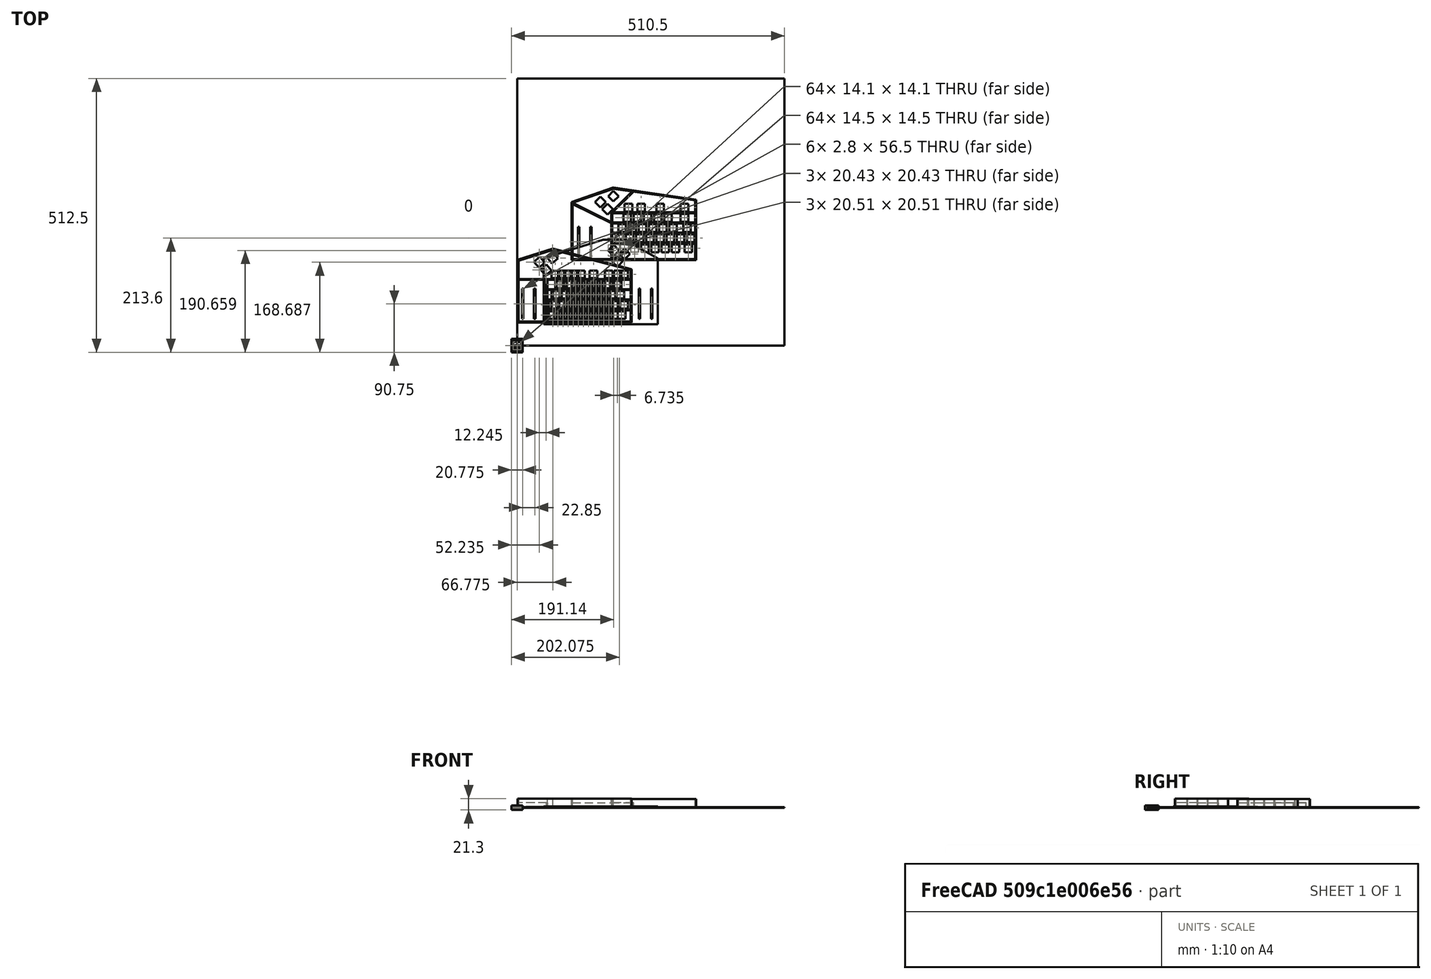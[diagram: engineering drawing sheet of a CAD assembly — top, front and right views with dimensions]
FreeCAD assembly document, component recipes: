
FREECAD ASSEMBLY — COMPONENT RECIPES ("keyboard")

This assembly document has 5 components, labeled P0..P4 below (a component is one placed body or linked part). 4 of them carry a construction recipe — the FreeCAD feature program that regenerates the part from scratch, quoted from this document or its linked companion documents; the rest are supplied as boundary geometry only. No exploded tour is included for this assembly.
COMPONENT P0 — recipe-attached ("Body", modeled in this document).
Construction recipe (the document's own serialized feature program — sketch geometry with constraints, then the solid features built on it; lengths are millimeters unless a unit is written):

FEATURE [Sketcher::SketchObject] Sketch
  FullyConstrained = true
  MapMode = 5
  Support = -> [XY_Plane001]
  sketch-geometry (8):
    g0: LineSegment StartX=-7.5 StartY=7.5 StartZ=0 EndX=7.5 EndY=7.5 EndZ=0
    g1: LineSegment StartX=7.5 StartY=7.5 StartZ=0 EndX=7.5 EndY=-7.5 EndZ=0
    g2: LineSegment StartX=7.5 StartY=-7.5 StartZ=0 EndX=-7.5 EndY=-7.5 EndZ=0
    g3: LineSegment StartX=-7.5 StartY=-7.5 StartZ=0 EndX=-7.5 EndY=7.5 EndZ=0
    g4: LineSegment StartX=-10.5 StartY=10.5 StartZ=0 EndX=10.5 EndY=10.5 EndZ=0
    g5: LineSegment StartX=10.5 StartY=10.5 StartZ=0 EndX=10.5 EndY=-10.5 EndZ=0
    g6: LineSegment StartX=10.5 StartY=-10.5 StartZ=0 EndX=-10.5 EndY=-10.5 EndZ=0
    g7: LineSegment StartX=-10.5 StartY=-10.5 StartZ=0 EndX=-10.5 EndY=10.5 EndZ=0
  constraints (20):
    c: Coincident(g0,g1)
    c: Coincident(g1,g2)
    c: Coincident(g2,g3)
    c: Coincident(g3,g0)
    c: Horizontal(g2)
    c: Vertical(g1)
    c: Symmetric(g0,g0,g-2)
    c: Symmetric(g0,g2,g-1)
    c: Equal(g0,g3)
    c: DistanceX(g0,g0) = 15
    c: Coincident(g4,g5)
    c: Coincident(g5,g6)
    c: Coincident(g6,g7)
    c: Coincident(g7,g4)
    c: Horizontal(g6)
    c: Vertical(g5)
    c: Symmetric(g4,g4,g-2)
    c: Symmetric(g4,g6,g-1)
    c: Equal(g4,g7)
    c: DistanceX(g4,g0) = 3
FEATURE [PartDesign::Pad] Pad
  Direction = (0,0,1)
  Length = 2.5
  Length2 = 10
  Profile = -> Sketch
  ReferenceAxis = -> Sketch [N_Axis]
  Type = 0
FEATURE [Sketcher::SketchObject] Sketch001
  ExternalGeometry = -> [Pad]
  FullyConstrained = true
  MapMode = 5
  Placement = pos=(0,0,0) rot=(1,0,0;3.14159rad)
  Support = -> [Pad]
  expr: Constraints[11] = 4.15 / 2
  sketch-geometry (5):
    g0: LineSegment StartX=-10.5 StartY=10.5 StartZ=0 EndX=10.5 EndY=10.5 EndZ=0
    g1: LineSegment StartX=10.5 StartY=10.5 StartZ=0 EndX=10.5 EndY=-10.5 EndZ=0
    g2: LineSegment StartX=10.5 StartY=-10.5 StartZ=0 EndX=-10.5 EndY=-10.5 EndZ=0
    g3: LineSegment StartX=-10.5 StartY=-10.5 StartZ=0 EndX=-10.5 EndY=10.5 EndZ=0
    g4: Circle CenterX=0 CenterY=0 CenterZ=0 NormalX=0 NormalY=0 NormalZ=1 AngleXU=0 Radius=2.075
  constraints (12):
    c: Coincident(g0,g1)
    c: Coincident(g1,g2)
    c: Coincident(g2,g3)
    c: Coincident(g3,g0)
    c: Horizontal(g0)
    c: Horizontal(g2)
    c: Vertical(g1)
    c: Vertical(g3)
    c: Coincident(g0,g-3)
    c: Coincident(g1,g-4)
    c: Coincident(g4,g-1)
    c: Radius(g4) = 2.075
FEATURE [PartDesign::Pad] Pad001
  BaseFeature = -> Pad
  Direction = (0,0,-1)
  Length = 4
  Length2 = 10
  Profile = -> Sketch001
  ReferenceAxis = -> Sketch001 [N_Axis]
  Type = 0
FEATURE [Sketcher::SketchObject] Sketch002
  ExternalGeometry = -> [Pad001]
  FullyConstrained = true
  MapMode = 5
  Placement = pos=(0,0,2.5) rot=(0,0,1;0rad)
  Support = -> [Pad001]
  sketch-geometry (8):
    g0: LineSegment StartX=-10.5 StartY=10.5 StartZ=0 EndX=10.5 EndY=10.5 EndZ=0
    g1: LineSegment StartX=10.5 StartY=10.5 StartZ=0 EndX=10.5 EndY=-10.5 EndZ=0
    g2: LineSegment StartX=10.5 StartY=-10.5 StartZ=0 EndX=-10.5 EndY=-10.5 EndZ=0
    g3: LineSegment StartX=-10.5 StartY=-10.5 StartZ=0 EndX=-10.5 EndY=10.5 EndZ=0
    g4: LineSegment StartX=-7.25 StartY=7.25 StartZ=0 EndX=7.25 EndY=7.25 EndZ=0
    g5: LineSegment StartX=7.25 StartY=7.25 StartZ=0 EndX=7.25 EndY=-7.25 EndZ=0
    g6: LineSegment StartX=7.25 StartY=-7.25 StartZ=0 EndX=-7.25 EndY=-7.25 EndZ=0
    g7: LineSegment StartX=-7.25 StartY=-7.25 StartZ=0 EndX=-7.25 EndY=7.25 EndZ=0
  constraints (20):
    c: Coincident(g0,g1)
    c: Coincident(g1,g2)
    c: Coincident(g2,g3)
    c: Coincident(g3,g0)
    c: Horizontal(g0)
    c: Horizontal(g2)
    c: Vertical(g1)
    c: Vertical(g3)
    c: Coincident(g0,g-3)
    c: Coincident(g1,g-4)
    c: Coincident(g4,g5)
    c: Coincident(g5,g6)
    c: Coincident(g6,g7)
    c: Coincident(g7,g4)
    c: Horizontal(g6)
    c: Vertical(g5)
    c: Symmetric(g4,g4,g-2)
    c: Symmetric(g4,g6,g-1)
    c: DistanceX(g4,g4) = 14.5
    c: Equal(g7,g4)
FEATURE [PartDesign::Pad] Pad002
  BaseFeature = -> Pad001
  Direction = (0,0,1)
  Length = 2.3
  Length2 = 10
  Profile = -> Sketch002
  ReferenceAxis = -> Sketch002 [N_Axis]
  Type = 0
FEATURE [PartDesign::Chamfer] Chamfer
  Angle = 45
  Base = -> Pad002 [Edge19,Edge23,Edge11,Edge12]
  BaseFeature = -> Pad002
  ChamferType = 0
  FlipDirection = false
  Size = 3
  Size2 = 1
  SupportTransform = false
  UseAllEdges = false
FEATURE [Sketcher::SketchObject] Sketch003
  FullyConstrained = true
  MapMode = 5
  Placement = pos=(0,0,-4) rot=(1,0,0;3.14159rad)
  Support = -> [Chamfer]
  sketch-geometry (2):
    g0: Circle CenterX=4 CenterY=2.85 CenterZ=0 NormalX=0 NormalY=0 NormalZ=1 AngleXU=0 Radius=0.75
    g1: Circle CenterX=-2.9 CenterY=5 CenterZ=0 NormalX=0 NormalY=0 NormalZ=1 AngleXU=0 Radius=0.75
  constraints (6):
    c: DistanceX(g-1,g0) = 4
    c: DistanceY(g-1,g0) = 2.85
    c: Radius(g0) = 0.75
    c: DistanceX(g1,g-1) = 2.9
    c: DistanceY(g-1,g1) = 5
    c: Equal(g1,g0)
FEATURE [PartDesign::Pocket] Pocket
  BaseFeature = -> Chamfer
  Direction = (0,0,1)
  Length = 5
  Length2 = 5
  Profile = -> Sketch003
  ReferenceAxis = -> Sketch003 [N_Axis]
  Type = 1
FEATURE [PartDesign::Chamfer] Chamfer001
  Angle = 45
  Base = -> Pocket [Edge27,Edge26]
  BaseFeature = -> Pocket
  ChamferType = 1
  FlipDirection = false
  Size = 1.8
  Size2 = 3.999
  SupportTransform = false
  UseAllEdges = false
FEATURE [PartDesign::Body] Body
  Group = -> [Sketch,Pad,Sketch001,Pad001,Sketch002,Pad002,Chamfer,Sketch003,Pocket,Chamfer001]
  Origin = -> Origin001
  Tip = -> Chamfer001
COMPONENT P1 — recipe-attached ("Body001", modeled in this document).
Construction recipe (the document's own serialized feature program — sketch geometry with constraints, then the solid features built on it; lengths are millimeters unless a unit is written):

FEATURE [Sketcher::SketchObject] Sketch004
  FullyConstrained = true
  MapMode = 5
  Support = -> [XY_Plane002]
  sketch-geometry (8):
    g0: LineSegment StartX=-7.5 StartY=7.5 StartZ=0 EndX=7.5 EndY=7.5 EndZ=0
    g1: LineSegment StartX=7.5 StartY=7.5 StartZ=0 EndX=7.5 EndY=-7.5 EndZ=0
    g2: LineSegment StartX=7.5 StartY=-7.5 StartZ=0 EndX=-7.5 EndY=-7.5 EndZ=0
    g3: LineSegment StartX=-7.5 StartY=-7.5 StartZ=0 EndX=-7.5 EndY=7.5 EndZ=0
    g4: LineSegment StartX=-10.5 StartY=10.5 StartZ=0 EndX=10.5 EndY=10.5 EndZ=0
    g5: LineSegment StartX=10.5 StartY=10.5 StartZ=0 EndX=10.5 EndY=-10.5 EndZ=0
    g6: LineSegment StartX=10.5 StartY=-10.5 StartZ=0 EndX=-10.5 EndY=-10.5 EndZ=0
    g7: LineSegment StartX=-10.5 StartY=-10.5 StartZ=0 EndX=-10.5 EndY=10.5 EndZ=0
  constraints (20):
    c: Coincident(g0,g1)
    c: Coincident(g1,g2)
    c: Coincident(g2,g3)
    c: Coincident(g3,g0)
    c: Horizontal(g2)
    c: Vertical(g1)
    c: Symmetric(g0,g0,g-2)
    c: Symmetric(g0,g2,g-1)
    c: Equal(g0,g3)
    c: DistanceX(g0,g0) = 15
    c: Coincident(g4,g5)
    c: Coincident(g5,g6)
    c: Coincident(g6,g7)
    c: Coincident(g7,g4)
    c: Horizontal(g6)
    c: Vertical(g5)
    c: Symmetric(g4,g4,g-2)
    c: Symmetric(g4,g6,g-1)
    c: Equal(g4,g7)
    c: DistanceX(g4,g0) = 3
FEATURE [PartDesign::Pad] Pad003
  Direction = (0,0,1)
  Length = 2.5
  Length2 = 10
  Profile = -> Sketch004
  ReferenceAxis = -> Sketch004 [N_Axis]
  Type = 0
FEATURE [Sketcher::SketchObject] Sketch005
  ExternalGeometry = -> [Pad003]
  FullyConstrained = true
  MapMode = 5
  Placement = pos=(0,0,0) rot=(1,0,0;3.14159rad)
  Support = -> [Pad003]
  expr: Constraints[11] = 4.15 / 2
  sketch-geometry (5):
    g0: LineSegment StartX=-10.5 StartY=10.5 StartZ=0 EndX=10.5 EndY=10.5 EndZ=0
    g1: LineSegment StartX=10.5 StartY=10.5 StartZ=0 EndX=10.5 EndY=-10.5 EndZ=0
    g2: LineSegment StartX=10.5 StartY=-10.5 StartZ=0 EndX=-10.5 EndY=-10.5 EndZ=0
    g3: LineSegment StartX=-10.5 StartY=-10.5 StartZ=0 EndX=-10.5 EndY=10.5 EndZ=0
    g4: Circle CenterX=0 CenterY=0 CenterZ=0 NormalX=0 NormalY=0 NormalZ=1 AngleXU=0 Radius=2.075
  constraints (12):
    c: Coincident(g0,g1)
    c: Coincident(g1,g2)
    c: Coincident(g2,g3)
    c: Coincident(g3,g0)
    c: Horizontal(g0)
    c: Horizontal(g2)
    c: Vertical(g1)
    c: Vertical(g3)
    c: Coincident(g0,g-3)
    c: Coincident(g1,g-4)
    c: Coincident(g4,g-1)
    c: Radius(g4) = 2.075
FEATURE [PartDesign::Pad] Pad004
  BaseFeature = -> Pad003
  Direction = (0,0,-1)
  Length = 4
  Length2 = 10
  Profile = -> Sketch005
  ReferenceAxis = -> Sketch005 [N_Axis]
  Type = 0
FEATURE [Sketcher::SketchObject] Sketch006
  ExternalGeometry = -> [Pad004]
  FullyConstrained = true
  MapMode = 5
  Placement = pos=(0,0,2.5) rot=(0,0,1;0rad)
  Support = -> [Pad004]
  sketch-geometry (8):
    g0: LineSegment StartX=-10.5 StartY=10.5 StartZ=0 EndX=10.5 EndY=10.5 EndZ=0
    g1: LineSegment StartX=10.5 StartY=10.5 StartZ=0 EndX=10.5 EndY=-10.5 EndZ=0
    g2: LineSegment StartX=10.5 StartY=-10.5 StartZ=0 EndX=-10.5 EndY=-10.5 EndZ=0
    g3: LineSegment StartX=-10.5 StartY=-10.5 StartZ=0 EndX=-10.5 EndY=10.5 EndZ=0
    g4: LineSegment StartX=-7.25 StartY=7.25 StartZ=0 EndX=7.25 EndY=7.25 EndZ=0
    g5: LineSegment StartX=7.25 StartY=7.25 StartZ=0 EndX=7.25 EndY=-7.25 EndZ=0
    g6: LineSegment StartX=7.25 StartY=-7.25 StartZ=0 EndX=-7.25 EndY=-7.25 EndZ=0
    g7: LineSegment StartX=-7.25 StartY=-7.25 StartZ=0 EndX=-7.25 EndY=7.25 EndZ=0
  constraints (20):
    c: Coincident(g0,g1)
    c: Coincident(g1,g2)
    c: Coincident(g2,g3)
    c: Coincident(g3,g0)
    c: Horizontal(g0)
    c: Horizontal(g2)
    c: Vertical(g1)
    c: Vertical(g3)
    c: Coincident(g0,g-3)
    c: Coincident(g1,g-4)
    c: Coincident(g4,g5)
    c: Coincident(g5,g6)
    c: Coincident(g6,g7)
    c: Coincident(g7,g4)
    c: Horizontal(g6)
    c: Vertical(g5)
    c: Symmetric(g4,g4,g-2)
    c: Symmetric(g4,g6,g-1)
    c: DistanceX(g4,g4) = 14.5
    c: Equal(g7,g4)
FEATURE [PartDesign::Pad] Pad005
  BaseFeature = -> Pad004
  Direction = (0,0,1)
  Length = 2.3
  Length2 = 10
  Profile = -> Sketch006
  ReferenceAxis = -> Sketch006 [N_Axis]
  Type = 0
FEATURE [Sketcher::SketchObject] Sketch007
  ExternalGeometry = -> [Pad005]
  FullyConstrained = true
  MapMode = 5
  Placement = pos=(0,0,-4) rot=(1,0,0;3.14159rad)
  Support = -> [Pad005]
  sketch-geometry (22):
    g0: LineSegment StartX=-7.5 StartY=6.5 StartZ=0 EndX=-2 EndY=6.5 EndZ=0
    g1: LineSegment StartX=-2 StartY=6.5 StartZ=0 EndX=-2 EndY=3.5 EndZ=0
    g2: LineSegment StartX=-2 StartY=3.5 StartZ=0 EndX=-7.5 EndY=3.5 EndZ=0
    g3: LineSegment StartX=-7.5 StartY=3.5 StartZ=0 EndX=-7.5 EndY=6.5 EndZ=0
    g4: LineSegment StartX=3 StartY=4.35 StartZ=0 EndX=7.5 EndY=4.35 EndZ=0
    g5: LineSegment StartX=7.5 StartY=4.35 StartZ=0 EndX=7.5 EndY=1.35 EndZ=0
    g6: LineSegment StartX=7.5 StartY=1.35 StartZ=0 EndX=3 EndY=1.35 EndZ=0
    g7: LineSegment StartX=3 StartY=1.35 StartZ=0 EndX=3 EndY=4.35 EndZ=0
    g8: Circle CenterX=-2.9 CenterY=5 CenterZ=0 NormalX=0 NormalY=0 NormalZ=1 AngleXU=0 Radius=0.75
    g9: Circle CenterX=4 CenterY=2.85 CenterZ=0 NormalX=0 NormalY=0 NormalZ=1 AngleXU=0 Radius=0.75
    g10: LineSegment StartX=-2.9 StartY=5 StartZ=0 EndX=-7.5 EndY=5 EndZ=0
    g11: LineSegment StartX=-7.5 StartY=5 StartZ=0 EndX=-7.5 EndY=6.5 EndZ=0
    g12: LineSegment StartX=-7.5 StartY=5 StartZ=0 EndX=-7.5 EndY=3.5 EndZ=0
    g13: LineSegment StartX=4 StartY=2.85 StartZ=0 EndX=7.5 EndY=2.85 EndZ=0
    g14: LineSegment StartX=7.5 StartY=2.85 StartZ=0 EndX=7.5 EndY=1.35 EndZ=0
    g15: LineSegment StartX=7.5 StartY=2.85 StartZ=0 EndX=7.5 EndY=4.35 EndZ=0
    g16: LineSegment StartX=3 StartY=4.35 StartZ=0 EndX=3.8 EndY=3.57284 EndZ=0
    g17: LineSegment StartX=3 StartY=1.35 StartZ=0 EndX=3.8 EndY=2.12716 EndZ=0
    g18: ArcOfCircle CenterX=4 CenterY=2.85 CenterZ=0 NormalX=0 NormalY=0 NormalZ=1 AngleXU=0 Radius=0.75 StartAngle=1.84073 EndAngle=4.44246
    g19: LineSegment StartX=-2 StartY=6.5 StartZ=0 EndX=-2.7 EndY=5.72284 EndZ=0
    g20: LineSegment StartX=-2 StartY=3.5 StartZ=0 EndX=-2.7 EndY=4.27716 EndZ=0
    g21: ArcOfCircle CenterX=-2.9 CenterY=5 CenterZ=0 NormalX=0 NormalY=0 NormalZ=1 AngleXU=0 Radius=0.75 StartAngle=4.98232 EndAngle=7.58405
  constraints (60):
    c: Coincident(g0,g1)
    c: Coincident(g1,g2)
    c: Coincident(g2,g3)
    c: Coincident(g3,g0)
    c: Horizontal(g0)
    c: Horizontal(g2)
    c: Vertical(g1)
    c: Vertical(g3)
    c: Coincident(g4,g5)
    c: Coincident(g5,g6)
    c: Coincident(g6,g7)
    c: Coincident(g7,g4)
    c: Horizontal(g4)
    c: Horizontal(g6)
    c: Vertical(g5)
    c: Vertical(g7)
    c: PointOnObject(g4,g-4)
    c: PointOnObject(g0,g-3)
    c: DistanceY(g-1,g9) = 2.85
    c: DistanceX(g-1,g9) = 4
    c: Radius(g9) = 0.75
    c: DistanceY(g-1,g8) = 5
    c: DistanceX(g8,g-1) = 2.9
    c: Radius(g8) = 0.75
    c: Coincident(g10,g8)
    c: PointOnObject(g10,g-3)
    c: Coincident(g11,g10)
    c: Equal(g12,g11)
    c: Coincident(g12,g10)
    c: Horizontal(g10)
    c: Coincident(g12,g2)
    c: Coincident(g11,g0)
    c: Coincident(g13,g9)
    c: PointOnObject(g13,g-4)
    c: Coincident(g14,g13)
    c: Coincident(g15,g13)
    c: Equal(g15,g14)
    c: Horizontal(g13)
    c: Coincident(g15,g4)
    c: Coincident(g14,g5)
    c: DistanceX(g6,g5) = 4.5
    c: DistanceX(g2,g2) = 5.5
    c: DistanceY(g1,g1) = 3
    c: Coincident(g16,g4)
    c: Coincident(g17,g6)
    c: Coincident(g18,g9)
    c: Coincident(g18,g16)
    c: Coincident(g18,g17)
    c: Equal(g18,g9)
    c: DistanceX(g17,g18) = 0.2
    c: Equal(g16,g17)
    c: Coincident(g19,g0)
    c: PointOnObject(g19,g8)
    c: Coincident(g20,g2)
    c: Coincident(g21,g8)
    c: Coincident(g21,g19)
    c: Coincident(g21,g20)
    c: Equal(g19,g20)
    c: DistanceX(g21,g20) = 0.2
    c: Equal(g1,g7)
FEATURE [PartDesign::Pocket] Pocket001
  BaseFeature = -> Pad005
  Direction = (0,0,1)
  Length = 0
  Length2 = 5
  Profile = -> Sketch007
  ReferenceAxis = -> Sketch007 [N_Axis]
  Type = 3
  UpToFace = -> Pad005 [Face20]
FEATURE [PartDesign::Fillet] Fillet
  Base = -> Pocket001 [Edge65,Edge68,Edge49,Edge53]
  BaseFeature = -> Pocket001
  Radius = 1
  SupportTransform = false
  UseAllEdges = false
FEATURE [Sketcher::SketchObject] Sketch008
  ExternalGeometry = -> [Fillet]
  FullyConstrained = true
  MapMode = 5
  Placement = pos=(0,0,4.8) rot=(0,0,1;0rad)
  Support = -> [Fillet]
  sketch-geometry (4):
    g0: LineSegment StartX=-10.5 StartY=0 StartZ=0 EndX=10.5 EndY=0 EndZ=0
    g1: LineSegment StartX=10.5 StartY=0 StartZ=0 EndX=10.5 EndY=-6.5 EndZ=0
    g2: LineSegment StartX=10.5 StartY=-6.5 StartZ=0 EndX=-10.5 EndY=-6.5 EndZ=0
    g3: LineSegment StartX=-10.5 StartY=-6.5 StartZ=0 EndX=-10.5 EndY=0 EndZ=0
  constraints (11):
    c: Coincident(g0,g1)
    c: Coincident(g1,g2)
    c: Coincident(g2,g3)
    c: Coincident(g3,g0)
    c: Horizontal(g2)
    c: Vertical(g1)
    c: Vertical(g3)
    c: PointOnObject(g0,g-1)
    c: PointOnObject(g2,g-3)
    c: Symmetric(g0,g0,g-2)
    c: PointOnObject(g2,g-4)
FEATURE [PartDesign::Pocket] Pocket002
  BaseFeature = -> Fillet
  Direction = (0,0,-1)
  Length = 0
  Length2 = 5
  Profile = -> Sketch008
  ReferenceAxis = -> Sketch008 [N_Axis]
  Type = 3
  UpToFace = -> Fillet [Face23]
FEATURE [PartDesign::Pad] Pad006
  BaseFeature = -> Pocket002
  Direction = (0,-1,0)
  Length = 2
  Length2 = 10
  Profile = -> Pocket002 [Face10,Face26,Face39]
  Type = 0
FEATURE [PartDesign::Pad] Pad007
  BaseFeature = -> Pad006
  Direction = (0,1,0)
  Length = 2
  Length2 = 10
  Profile = -> Pad006 [Face13,Face34,Face50]
  Type = 0
FEATURE [PartDesign::CoordinateSystem] Local_CS
  AttacherType = Attacher::AttachEngine3D
  MapMode = 45
  Placement = pos=(3.31163,-2.85,0) rot=(0,0.707107,0.707107;3.14159rad)
  Support = -> [Pad007]
FEATURE [PartDesign::CoordinateSystem] Local_CS001
  AttacherType = Attacher::AttachEngine3D
  MapMode = 45
  Placement = pos=(-2.22398,-5,0) rot=(0,0.707107,0.707107;3.14159rad)
  Support = -> [Pad007]
FEATURE [PartDesign::Body] Body001
  Group = -> [Sketch004,Pad003,Sketch005,Pad004,Sketch006,Pad005,Sketch007,Pocket001,Fillet,Sketch008,Pocket002,Pad006,Pad007,Local_CS,Local_CS001]
  Origin = -> Origin002
  Tip = -> Pad007
COMPONENT P2 — geometry summary ("Model"; no construction recipe available for this part):
  bounding box: 16.1 x 4.1 x 4.0 mm
  tessellated surface: 228 triangles
  volume: 2451513960528901609903646099353169505613957827253961644439277037358750804026721693641421339358597268239748682215783712032644430022589533140220938276317429760 mm^3 (915252545422869498662315967676567421757163301824653543720582276189938750638123076976993345633309426533124652158865058795889452386300277657998858502413484032% of its bounding box)
  symmetry: 2-fold rotationally symmetric about the z axis
COMPONENT P3 — recipe-attached ("spring", modeled in this document).
Construction recipe (the document's own serialized feature program — sketch geometry with constraints, then the solid features built on it; lengths are millimeters unless a unit is written):

FEATURE [Sketcher::SketchObject] Sketch013
  FullyConstrained = true
  MapMode = 5
  Support = -> [XY_Plane008]
  sketch-geometry (6):
    g0: ArcOfCircle CenterX=-0.866025 CenterY=0 CenterZ=0 NormalX=0 NormalY=0 NormalZ=1 AngleXU=0 Radius=1 StartAngle=5.75959 EndAngle=6.80678
    g1: LineSegment StartX=0 StartY=0.5 StartZ=0 EndX=0 EndY=1 EndZ=0
    g2: LineSegment StartX=0 StartY=1 StartZ=0 EndX=1 EndY=1 EndZ=0
    g3: LineSegment StartX=1 StartY=1 StartZ=0 EndX=1 EndY=-1 EndZ=0
    g4: LineSegment StartX=1 StartY=-1 StartZ=0 EndX=0 EndY=-1 EndZ=0
    g5: LineSegment StartX=0 StartY=-1 StartZ=0 EndX=2e-16 EndY=-0.5 EndZ=0
  constraints (19):
    c: PointOnObject(g0,g-1)
    c: PointOnObject(g0,g-2)
    c: PointOnObject(g0,g-2)
    c: Coincident(g1,g2)
    c: Horizontal(g2)
    c: Coincident(g2,g3)
    c: Coincident(g3,g4)
    c: PointOnObject(g4,g-2)
    c: Horizontal(g4)
    c: Coincident(g4,g5)
    c: Coincident(g5,g0)
    c: PointOnObject(g1,g-2)
    c: Vertical(g3)
    c: DistanceY(g3,g3) = 2
    c: Radius(g0) = 1
    c: Coincident(g1,g0)
    c: Equal(g1,g5)
    c: DistanceY(g0,g0) = 1
    c: DistanceX(g2,g2) = 1
FEATURE [PartDesign::Pad] Pad011
  Direction = (0,0,1)
  Length = 4
  Length2 = 10
  Profile = -> Sketch013
  ReferenceAxis = -> Sketch013 [N_Axis]
  Reversed = true
  Type = 0
FEATURE [Sketcher::SketchObject] Sketch014
  ExternalGeometry = -> [Pad011]
  FullyConstrained = true
  MapMode = 5
  Support = -> [XY_Plane008]
  sketch-geometry (21):
    g0: LineSegment StartX=1 StartY=1 StartZ=0 EndX=1.66667 EndY=-0.8 EndZ=0
    g1: LineSegment StartX=1.66667 StartY=-0.8 StartZ=0 EndX=2.33333 EndY=1 EndZ=0
    g2: LineSegment StartX=2.33333 StartY=1 StartZ=0 EndX=3 EndY=-0.8 EndZ=0
    g3: LineSegment StartX=3 StartY=-0.8 StartZ=0 EndX=3.66667 EndY=1 EndZ=0
    g4: LineSegment StartX=3.66667 StartY=1 StartZ=0 EndX=4.33333 EndY=-0.8 EndZ=0
    g5: LineSegment StartX=4.33333 StartY=-0.8 StartZ=0 EndX=5 EndY=1 EndZ=0
    g6: LineSegment StartX=1 StartY=1 StartZ=0 EndX=5 EndY=1 EndZ=0
    g7: LineSegment StartX=1 StartY=-1 StartZ=0 EndX=4.33333 EndY=-1 EndZ=0
    g8: LineSegment StartX=1 StartY=0.8 StartZ=0 EndX=1.66667 EndY=-1 EndZ=0
    g9: LineSegment StartX=1.66667 StartY=-1 StartZ=0 EndX=2.33333 EndY=0.8 EndZ=0
    g10: LineSegment StartX=2.33333 StartY=0.8 StartZ=0 EndX=3 EndY=-1 EndZ=0
    g11: LineSegment StartX=3 StartY=-1 StartZ=0 EndX=3.66667 EndY=0.8 EndZ=0
    g12: LineSegment StartX=3.66667 StartY=0.8 StartZ=0 EndX=4.33333 EndY=-1 EndZ=0
    g13: LineSegment StartX=4.33333 StartY=-1 StartZ=0 EndX=5 EndY=0.8 EndZ=0
    g14: LineSegment StartX=1.66667 StartY=-0.8 StartZ=0 EndX=1.66667 EndY=-1 EndZ=0
    g15: LineSegment StartX=3 StartY=-0.8 StartZ=0 EndX=3 EndY=-1 EndZ=0
    g16: LineSegment StartX=2.33333 StartY=0.8 StartZ=0 EndX=2.33333 EndY=1 EndZ=0
    g17: LineSegment StartX=3.66667 StartY=0.8 StartZ=0 EndX=3.66667 EndY=1 EndZ=0
    g18: LineSegment StartX=5 StartY=0.8 StartZ=0 EndX=5 EndY=1 EndZ=0
    g19: LineSegment StartX=4.33333 StartY=-0.8 StartZ=0 EndX=4.33333 EndY=-1 EndZ=0
    g20: LineSegment StartX=1 StartY=0.8 StartZ=0 EndX=1 EndY=1 EndZ=0
  constraints (55):
    c: Coincident(g-3,g0)
    c: Coincident(g0,g1)
    c: Coincident(g1,g2)
    c: Coincident(g2,g3)
    c: Coincident(g3,g4)
    c: Coincident(g6,g0)
    c: Coincident(g6,g5)
    c: Coincident(g7,g-3)
    c: Horizontal(g7)
    c: Horizontal(g6)
    c: PointOnObject(g3,g6)
    c: PointOnObject(g1,g6)
    c: Coincident(g5,g4)
    c: PointOnObject(g8,g-3)
    c: PointOnObject(g8,g7)
    c: Coincident(g8,g9)
    c: Coincident(g9,g10)
    c: PointOnObject(g10,g7)
    c: Coincident(g10,g11)
    c: Coincident(g11,g12)
    c: Coincident(g12,g7)
    c: Coincident(g12,g13)
    c: Coincident(g14,g0)
    c: Coincident(g14,g8)
    c: Coincident(g15,g2)
    c: Coincident(g15,g10)
    c: Coincident(g16,g9)
    c: Coincident(g16,g1)
    c: Coincident(g17,g11)
    c: Coincident(g17,g3)
    c: Vertical(g17)
    c: Coincident(g18,g13)
    c: Coincident(g18,g5)
    c: Coincident(g19,g4)
    c: Coincident(g19,g12)
    c: Equal(g14,g16)
    c: Equal(g16,g15)
    c: Equal(g15,g17)
    c: Equal(g17,g19)
    c: Equal(g19,g18)
    c: Vertical(g14)
    c: Vertical(g16)
    c: Vertical(g15)
    c: Vertical(g18)
    c: Vertical(g19)
    c: Equal(g0,g1)
    c: Equal(g2,g3)
    c: Equal(g3,g4)
    c: Equal(g4,g5)
    c: Equal(g5,g8)
    c: Equal(g8,g9)
    c: Coincident(g20,g8)
    c: Coincident(g20,g0)
    c: DistanceY(g18,g18) = 0.2
    c: DistanceX(g6,g6) = 4
FEATURE [PartDesign::Pad] Pad012
  BaseFeature = -> Pad011
  Direction = (0,0,1)
  Length = 4
  Length2 = 10
  Profile = -> Sketch014
  ReferenceAxis = -> Sketch014 [N_Axis]
  Reversed = true
  Type = 0
FEATURE [PartDesign::Pocket] Pocket006
  BaseFeature = -> Pad012
  Direction = (0,0,-1)
  Length = 1
  Length2 = 5
  Profile = -> Pad012 [Face8]
  Type = 0
FEATURE [Sketcher::SketchObject] Sketch020
  FullyConstrained = true
  MapMode = 5
  Placement = pos=(1,0,0) rot=(0.57735,0.57735,0.57735;2.0944rad)
  Support = -> [Pocket006]
  sketch-geometry (1):
    g0: Circle CenterX=0 CenterY=-0.3 CenterZ=0 NormalX=0 NormalY=0 NormalZ=1 AngleXU=0 Radius=0.65
  constraints (3):
    c: PointOnObject(g0,g-2)
    c: Radius(g0) = 0.65
    c: DistanceY(g0,g-1) = 0.3
FEATURE [PartDesign::Pocket] Pocket007
  BaseFeature = -> Pocket006
  Direction = (-1,0,0)
  Length = 5
  Length2 = 5
  Profile = -> Sketch020
  ReferenceAxis = -> Sketch020 [N_Axis]
  Type = 1
FEATURE [PartDesign::Body] Body_2
  Group = -> [Sketch013,Pad011,Sketch014,Pad012,Pocket006,Sketch020,Pocket007]
  Origin = -> Origin008
  Tip = -> Pocket007
COMPONENT P4 — recipe-attached ("switch_plate", modeled in this document).
Construction recipe (the document's own serialized feature program — sketch geometry with constraints, then the solid features built on it; lengths are millimeters unless a unit is written):

FEATURE [PartDesign::CoordinateSystem] LCS_0004
  AttacherType = Attacher::AttachEngine3D
  MapMode = 2
  Support = -> [X_Axis012]
FEATURE [PartDesign::FeatureBase] BaseFeature
  BaseFeature = -> baseplate_left001001_solid
FEATURE [Sketcher::SketchObject] Sketch021
  ExternalGeometry = -> [BaseFeature]
  FullyConstrained = true
  MapMode = 5
  Placement = pos=(0,0,0) rot=(0,1,0;3.14159rad)
  Support = -> [XY_Plane012]
  sketch-geometry (16):
    g0: LineSegment StartX=-211.098 StartY=171.423 StartZ=0 EndX=-187.375 EndY=147.7 EndZ=0
    g1: LineSegment StartX=-211.098 StartY=171.423 StartZ=0 EndX=-200.845 EndY=181.676 EndZ=0
    g2: LineSegment StartX=-200.845 StartY=181.676 StartZ=0 EndX=-190.592 EndY=171.423 EndZ=0
    g3: LineSegment StartX=-190.592 StartY=171.423 StartZ=0 EndX=-200.845 EndY=161.17 EndZ=0
    g4: LineSegment StartX=-200.845 StartY=161.17 StartZ=0 EndX=-211.098 EndY=171.423 EndZ=0
    g5: LineSegment StartX=-187.375 StartY=147.7 StartZ=0 EndX=-177.122 EndY=157.953 EndZ=0
    g6: LineSegment StartX=-177.122 StartY=157.953 StartZ=0 EndX=-187.375 EndY=168.206 EndZ=0
    g7: LineSegment StartX=-187.375 StartY=168.206 StartZ=0 EndX=-197.628 EndY=157.953 EndZ=0
    g8: LineSegment StartX=-197.628 StartY=157.953 StartZ=0 EndX=-187.375 EndY=147.7 EndZ=0
    g9: LineSegment StartX=-180.64 StartY=167.906 StartZ=0 EndX=-170.387 EndY=178.159 EndZ=0
    g10: LineSegment StartX=-170.387 StartY=178.159 StartZ=0 EndX=-180.64 EndY=188.412 EndZ=0
    g11: LineSegment StartX=-180.64 StartY=188.412 StartZ=0 EndX=-190.893 EndY=178.159 EndZ=0
    g12: LineSegment StartX=-190.893 StartY=178.159 StartZ=0 EndX=-180.64 EndY=167.906 EndZ=0
    g13: LineSegment StartX=-190.592 StartY=171.423 StartZ=0 EndX=-187.375 EndY=174.641 EndZ=0
    g14: LineSegment StartX=-200.845 StartY=181.676 StartZ=0 EndX=-190.893 EndY=178.159 EndZ=0
    g15: LineSegment StartX=-180.64 StartY=167.906 StartZ=0 EndX=-177.122 EndY=157.953 EndZ=0
  constraints (45):
    c: Coincident(g1,g2)
    c: Coincident(g2,g3)
    c: Coincident(g3,g4)
    c: Coincident(g4,g1)
    c: PointOnObject(g3,g0)
    c: Equal(g4,g3)
    c: Equal(g3,g1)
    c: Equal(g1,g2)
    c: Perpendicular(g4,g1)
    c: Distance(g1) = 14.5
    c: Coincident(g0,g1)
    c: Coincident(g0,g5)
    c: Coincident(g5,g6)
    c: Coincident(g6,g7)
    c: PointOnObject(g7,g0)
    c: Coincident(g7,g8)
    c: Coincident(g8,g5)
    c: Equal(g7,g8)
    c: Equal(g8,g6)
    c: Equal(g6,g5)
    c: Equal(g5,g4)
    c: Perpendicular(g8,g7)
    c: Distance(g1,g7) = 19.05
    c: Coincident(g9,g10)
    c: Coincident(g10,g11)
    c: Coincident(g11,g12)
    c: Coincident(g12,g9)
    c: Equal(g11,g12)
    c: Equal(g12,g10)
    c: Equal(g10,g9)
    c: Perpendicular(g12,g11)
    c: Parallel(g2,g12)
    c: Coincident(g13,g2)
    c: PointOnObject(g13,g12)
    c: Perpendicular(g12,g13)
    c: Distance(g13,g3) = 19.05
    c: Coincident(g14,g1)
    c: Coincident(g14,g11)
    c: Coincident(g15,g9)
    c: Coincident(g15,g5)
    c: Equal(g15,g14)
    c: Equal(g6,g10)
    c: Angle(g8,g-1) = 0.785398
    c: DistanceX(g-3,g5) = 20
    c: DistanceY(g-3,g5) = 7
FEATURE [PartDesign::Pocket] Pocket012
  BaseFeature = -> BaseFeature
  Direction = (0,0,1)
  Length = 5
  Length2 = 5
  Profile = -> Sketch021
  ReferenceAxis = -> Sketch021 [N_Axis]
  Type = 0
FEATURE [Sketcher::SketchObject] Sketch022
  ExternalGeometry = -> [Pocket012]
  FullyConstrained = false
  MapMode = 5
  Placement = pos=(0,0,2.3) rot=(0,0,1;0rad)
  Support = -> [Pocket012]
  sketch-geometry (22):
    g0: LineSegment StartX=160.64 StartY=198.412 StartZ=0 EndX=200.64 EndY=198.412 EndZ=0
    g1: LineSegment StartX=49.525 StartY=40 StartZ=0 EndX=263.025 EndY=40 EndZ=0
    g2: LineSegment StartX=227.375 StartY=106.5 StartZ=0 EndX=230.175 EndY=106.5 EndZ=0
    g3: LineSegment StartX=230.175 StartY=106.5 StartZ=0 EndX=230.175 EndY=50 EndZ=0
    g4: LineSegment StartX=230.175 StartY=50 StartZ=0 EndX=227.375 EndY=50 EndZ=0
    g5: LineSegment StartX=227.375 StartY=50 StartZ=0 EndX=227.375 EndY=106.5 EndZ=0
    g6: LineSegment StartX=253.025 StartY=106.5 StartZ=0 EndX=250.225 EndY=106.5 EndZ=0
    g7: LineSegment StartX=250.225 StartY=106.5 StartZ=0 EndX=250.225 EndY=50 EndZ=0
    g8: LineSegment StartX=250.225 StartY=50 StartZ=0 EndX=253.025 EndY=50 EndZ=0
    g9: LineSegment StartX=253.025 StartY=50 StartZ=0 EndX=253.025 EndY=106.5 EndZ=0
    g10: LineSegment StartX=227.375 StartY=106.5 StartZ=0 EndX=228.775 EndY=106.5 EndZ=0
    g11: LineSegment StartX=228.775 StartY=106.5 StartZ=0 EndX=230.175 EndY=106.5 EndZ=0
    g12: LineSegment StartX=253.025 StartY=106.5 StartZ=0 EndX=251.625 EndY=106.5 EndZ=0
    g13: LineSegment StartX=251.625 StartY=106.5 StartZ=0 EndX=250.225 EndY=106.5 EndZ=0
    g14: LineSegment StartX=200.64 StartY=198.412 StartZ=0 EndX=263.025 EndY=163.412 EndZ=0
    g15: LineSegment StartX=263.025 StartY=163.412 StartZ=0 EndX=263.025 EndY=40 EndZ=0
    g16: LineSegment StartX=49.525 StartY=40 StartZ=0 EndX=49.525 EndY=163.412 EndZ=0
    g17: LineSegment StartX=49.525 StartY=163.412 StartZ=0 EndX=160.64 EndY=198.412 EndZ=0
    g18: LineSegment StartX=0 StartY=0 StartZ=0 EndX=511.801 EndY=0 EndZ=0
    g19: LineSegment StartX=511.801 StartY=0 StartZ=0 EndX=511.801 EndY=507.959 EndZ=0
    g20: LineSegment StartX=511.801 StartY=507.959 StartZ=0 EndX=0 EndY=507.959 EndZ=0
    g21: LineSegment StartX=0 StartY=507.959 StartZ=0 EndX=0 EndY=0 EndZ=0
  constraints (61):
    c: Coincident(g0,g14)
    c: Coincident(g17,g0)
    c: Coincident(g1,g15)
    c: Coincident(g2,g3)
    c: Coincident(g3,g4)
    c: Coincident(g4,g5)
    c: Coincident(g5,g2)
    c: Horizontal(g2)
    c: Horizontal(g4)
    c: Vertical(g3)
    c: Vertical(g5)
    c: Coincident(g6,g7)
    c: Coincident(g7,g8)
    c: Coincident(g8,g9)
    c: Coincident(g9,g6)
    c: Horizontal(g6)
    c: Horizontal(g8)
    c: Vertical(g7)
    c: Vertical(g9)
    c: Coincident(g10,g2)
    c: Coincident(g11,g10)
    c: Coincident(g11,g2)
    c: Equal(g11,g10)
    c: PointOnObject(g10,g2)
    c: Coincident(g6,g12)
    c: Coincident(g12,g13)
    c: Coincident(g13,g6)
    c: Equal(g13,g12)
    c: PointOnObject(g12,g6)
    c: DistanceX(g10,g12) = 22.85
    c: Equal(g2,g6)
    c: DistanceX(g4,g4) = 2.8
    c: DistanceY(g5,g5) = 56.5
    c: PointOnObject(g6,g2)
    c: PointOnObject(g8,g4)
    c: Horizontal(g1)
    c: DistanceX(g-3,g2) = 20
    c: DistanceY(g4,g-4) = 0
    c: DistanceY(g15,g-4) = 10
    c: DistanceX(g16,g-6) = 10
    c: DistanceX(g8,g15) = 10
    c: Coincident(g14,g15)
    c: Vertical(g15)
    c: Horizontal(g0)
    c: DistanceY(g-5,g0) = 10
    c: Coincident(g16,g17)
    c: Vertical(g16)
    c: DistanceY(g16,g-5) = 25
    c: DistanceY(g14,g-5) = 25
    c: DistanceX(g0,g-5) = 20
    c: DistanceX(g-5,g0) = 20
    c: Coincident(g1,g16)
    c: Coincident(g18,g19)
    c: Coincident(g19,g20)
    c: Coincident(g20,g21)
    c: Coincident(g21,g18)
    c: Horizontal(g18)
    c: Horizontal(g20)
    c: Vertical(g19)
    c: Vertical(g21)
    c: Coincident(g18,g-1)
FEATURE [PartDesign::Pocket] Pocket013
  BaseFeature = -> Pocket012
  Direction = (0,0,-1)
  Length = 5
  Length2 = 5
  Profile = -> Sketch022
  ReferenceAxis = -> Sketch022 [N_Axis]
  Type = 0
FEATURE [PartDesign::CoordinateSystem] LCS_0005
  AttacherType = Attacher::AttachEngine3D
  MapMode = 2
  Support = -> [X_Axis]
FEATURE [PartDesign::FeatureBase] BaseFeature001
  BaseFeature = -> baseplate_right001001_solid
FEATURE [Sketcher::SketchObject] Sketch024
  ExternalGeometry = -> [BaseFeature001]
  FullyConstrained = true
  MapMode = 5
  Placement = pos=(0,0,0) rot=(1,0,0;3.14159rad)
  Support = -> [BaseFeature001]
  expr: Constraints[40] = 1.25 * 19.05
  sketch-geometry (16):
    g0: LineSegment StartX=42.6282 StartY=-166.401 StartZ=0 EndX=64.1937 EndY=-140.7 EndZ=0
    g1: LineSegment StartX=42.6282 StartY=-166.401 StartZ=0 EndX=31.5206 EndY=-157.08 EndZ=0
    g2: LineSegment StartX=31.5206 StartY=-157.08 StartZ=0 EndX=40.841 EndY=-145.973 EndZ=0
    g3: LineSegment StartX=40.841 StartY=-145.973 StartZ=0 EndX=51.9486 EndY=-155.293 EndZ=0
    g4: LineSegment StartX=51.9486 StartY=-155.293 StartZ=0 EndX=42.6282 EndY=-166.401 EndZ=0
    g5: LineSegment StartX=54.8733 StartY=-151.808 StartZ=0 EndX=43.7657 EndY=-142.487 EndZ=0
    g6: LineSegment StartX=43.7657 StartY=-142.487 StartZ=0 EndX=53.0861 EndY=-131.38 EndZ=0
    g7: LineSegment StartX=53.0861 StartY=-131.38 StartZ=0 EndX=64.1937 EndY=-140.7 EndZ=0
    g8: LineSegment StartX=64.1937 StartY=-140.7 StartZ=0 EndX=54.8733 EndY=-151.808 EndZ=0
    g9: LineSegment StartX=42.6282 StartY=-166.401 StartZ=0 EndX=53.411 EndY=-153.55 EndZ=0
    g10: LineSegment StartX=53.411 StartY=-153.55 StartZ=0 EndX=64.1937 EndY=-140.7 EndZ=0
    g11: LineSegment StartX=53.411 StartY=-153.55 StartZ=0 EndX=71.6524 EndY=-168.857 EndZ=0
    g12: LineSegment StartX=65.205 StartY=-153.983 StartZ=0 EndX=76.3126 EndY=-163.303 EndZ=0
    g13: LineSegment StartX=76.3126 StartY=-163.303 StartZ=0 EndX=66.9922 EndY=-174.411 EndZ=0
    g14: LineSegment StartX=66.9922 StartY=-174.411 StartZ=0 EndX=55.8846 EndY=-165.09 EndZ=0
    g15: LineSegment StartX=55.8846 StartY=-165.09 StartZ=0 EndX=65.205 EndY=-153.983 EndZ=0
  constraints (44):
    c: Coincident(g0,g1)
    c: Coincident(g1,g2)
    c: Coincident(g2,g3)
    c: PointOnObject(g3,g0)
    c: Coincident(g3,g4)
    c: Coincident(g4,g1)
    c: PointOnObject(g5,g0)
    c: Coincident(g5,g6)
    c: Coincident(g6,g7)
    c: Coincident(g7,g0)
    c: Coincident(g7,g8)
    c: Coincident(g8,g5)
    c: Equal(g1,g2)
    c: Equal(g2,g3)
    c: Equal(g3,g4)
    c: Equal(g4,g5)
    c: Equal(g5,g6)
    c: Equal(g6,g7)
    c: Equal(g7,g8)
    c: Perpendicular(g8,g5)
    c: Perpendicular(g4,g1)
    c: Distance(g1,g5) = 19.05
    c: Distance(g2) = 14.5
    c: Coincident(g9,g1)
    c: Coincident(g10,g9)
    c: Coincident(g10,g7)
    c: Equal(g9,g10)
    c: PointOnObject(g9,g0)
    c: Coincident(g11,g9)
    c: Perpendicular(g0,g11)
    c: Coincident(g12,g13)
    c: Coincident(g13,g14)
    c: Coincident(g14,g15)
    c: Coincident(g15,g12)
    c: Symmetric(g12,g14,g11)
    c: Symmetric(g12,g13,g11)
    c: Equal(g12,g15)
    c: Equal(g14,g13)
    c: Equal(g13,g8)
    c: PointOnObject(g11,g13)
    c: Distance(g11,g9) = 23.8125
    c: Angle(g7,g-3) = 0.698132
    c: DistanceX(g7,g-3) = 12
    c: PointOnObject(g7,g-3)
FEATURE [PartDesign::Pocket] Pocket014
  BaseFeature = -> BaseFeature001
  Direction = (0,0,1)
  Length = 5
  Length2 = 5
  Profile = -> Sketch024
  ReferenceAxis = -> Sketch024 [N_Axis]
  Type = 0
FEATURE [Sketcher::SketchObject] Sketch025
  ExternalGeometry = -> [Pocket014]
  FullyConstrained = true
  MapMode = 5
  Placement = pos=(0,0,0) rot=(1,0,0;3.14159rad)
  Support = -> [Pocket014]
  sketch-geometry (24):
    g0: LineSegment StartX=0.875002 StartY=-43 StartZ=0 EndX=214.375 EndY=-43 EndZ=0
    g1: LineSegment StartX=214.375 StartY=-43 StartZ=0 EndX=214.375 EndY=-143.007 EndZ=0
    g2: LineSegment StartX=214.375 StartY=-143.007 StartZ=0 EndX=66.9922 EndY=-181.411 EndZ=0
    g3: LineSegment StartX=66.9922 StartY=-181.411 StartZ=0 EndX=0.875002 EndY=-160.593 EndZ=0
    g4: LineSegment StartX=0.875002 StartY=-160.593 StartZ=0 EndX=0.875002 EndY=-43 EndZ=0
    g5: LineSegment StartX=42.6282 StartY=-166.401 StartZ=0 EndX=40.526 EndY=-173.078 EndZ=0
    g6: LineSegment StartX=66.9922 StartY=-181.411 StartZ=0 EndX=66.9922 EndY=-174.411 EndZ=0
    g7: LineSegment StartX=195.469 StartY=-140.7 StartZ=0 EndX=197.234 EndY=-147.474 EndZ=0
    g8: LineSegment StartX=8.875 StartY=-50 StartZ=0 EndX=11.675 EndY=-50 EndZ=0
    g9: LineSegment StartX=11.675 StartY=-50 StartZ=0 EndX=11.675 EndY=-106.5 EndZ=0
    g10: LineSegment StartX=11.675 StartY=-106.5 StartZ=0 EndX=8.875 EndY=-106.5 EndZ=0
    g11: LineSegment StartX=8.875 StartY=-106.5 StartZ=0 EndX=8.875 EndY=-50 EndZ=0
    g12: LineSegment StartX=31.725 StartY=-50 StartZ=0 EndX=34.525 EndY=-50 EndZ=0
    g13: LineSegment StartX=34.525 StartY=-50 StartZ=0 EndX=34.525 EndY=-106.5 EndZ=0
    g14: LineSegment StartX=34.525 StartY=-106.5 StartZ=0 EndX=31.725 EndY=-106.5 EndZ=0
    g15: LineSegment StartX=31.725 StartY=-106.5 StartZ=0 EndX=31.725 EndY=-50 EndZ=0
    g16: LineSegment StartX=8.875 StartY=-50 StartZ=0 EndX=10.275 EndY=-50 EndZ=0
    g17: LineSegment StartX=10.275 StartY=-50 StartZ=0 EndX=11.675 EndY=-50 EndZ=0
    g18: LineSegment StartX=31.725 StartY=-50 StartZ=0 EndX=33.125 EndY=-50 EndZ=0
    g19: LineSegment StartX=33.125 StartY=-50 StartZ=0 EndX=34.525 EndY=-50 EndZ=0
    g20: LineSegment StartX=0 StartY=0 StartZ=0 EndX=798.95 EndY=0 EndZ=0
    g21: LineSegment StartX=798.95 StartY=0 StartZ=0 EndX=798.95 EndY=-762.419 EndZ=0
    g22: LineSegment StartX=798.95 StartY=-762.419 StartZ=0 EndX=0 EndY=-762.419 EndZ=0
    g23: LineSegment StartX=0 StartY=-762.419 StartZ=0 EndX=0 EndY=0 EndZ=0
  constraints (68):
    c: Horizontal(g0)
    c: Coincident(g0,g1)
    c: Vertical(g1)
    c: Coincident(g1,g2)
    c: Coincident(g2,g3)
    c: Coincident(g3,g4)
    c: Coincident(g4,g0)
    c: Vertical(g4)
    c: DistanceX(g-3,g1) = 7
    c: Coincident(g5,g-4)
    c: PointOnObject(g5,g3)
    c: Perpendicular(g3,g5)
    c: Distance(g5) = 7
    c: Coincident(g6,g2)
    c: Coincident(g6,g-5)
    c: Vertical(g6)
    c: DistanceY(g6,g6) = 7
    c: Coincident(g7,g-6)
    c: PointOnObject(g7,g2)
    c: Perpendicular(g2,g7)
    c: Distance(g7) = 7
    c: DistanceY(g-7,g0) = 7
    c: Coincident(g8,g9)
    c: Coincident(g9,g10)
    c: Coincident(g10,g11)
    c: Coincident(g11,g8)
    c: Horizontal(g8)
    c: Horizontal(g10)
    c: Vertical(g9)
    c: Vertical(g11)
    c: Coincident(g12,g13)
    c: Coincident(g13,g14)
    c: Coincident(g14,g15)
    c: Coincident(g15,g12)
    c: Horizontal(g12)
    c: Horizontal(g14)
    c: Vertical(g13)
    c: Vertical(g15)
    c: Coincident(g16,g8)
    c: Coincident(g17,g16)
    c: Coincident(g17,g8)
    c: Equal(g17,g16)
    c: Horizontal(g16)
    c: Coincident(g12,g18)
    c: Coincident(g18,g19)
    c: Coincident(g19,g12)
    c: Equal(g19,g18)
    c: Horizontal(g19)
    c: PointOnObject(g8,g12)
    c: Equal(g11,g15)
    c: Equal(g10,g14)
    c: DistanceX(g16,g18) = 22.85
    c: DistanceY(g11,g11) = 56.5
    c: DistanceX(g10,g10) = 2.8
    c: DistanceY(g8,g0) = 7
    c: DistanceX(g0,g8) = 8
    c: Coincident(g20,g21)
    c: Coincident(g21,g22)
    c: Coincident(g22,g23)
    c: Coincident(g23,g20)
    c: Horizontal(g20)
    c: Horizontal(g22)
    c: Vertical(g21)
    c: Vertical(g23)
    c: Coincident(g20,g-1)
    c: DistanceX(g21) = 798.95
    c: DistanceY(g21) = -762.419
    c: DistanceX(g12,g-8) = 25
FEATURE [PartDesign::Pocket] Pocket015
  BaseFeature = -> Pocket014
  Direction = (0,0,1)
  Length = 5
  Length2 = 5
  Profile = -> Sketch025
  ReferenceAxis = -> Sketch025 [N_Axis]
  Type = 0
FEATURE [Sketcher::SketchObject] Sketch026
  ExternalGeometry = -> [Pocket015]
  FullyConstrained = true
  MapMode = 5
  Placement = pos=(0,0,2.3) rot=(0,0,1;0rad)
  Support = -> [Pocket015]
  sketch-geometry (10):
    g0: LineSegment StartX=0.875002 StartY=160.593 StartZ=0 EndX=66.9922 EndY=181.411 EndZ=0
    g1: LineSegment StartX=66.9922 StartY=181.411 StartZ=0 EndX=214.375 EndY=143.007 EndZ=0
    g2: LineSegment StartX=214.375 StartY=143.007 StartZ=0 EndX=214.375 EndY=43 EndZ=0
    g3: LineSegment StartX=214.375 StartY=43 StartZ=0 EndX=0.875002 EndY=43 EndZ=0
    g4: LineSegment StartX=0.875002 StartY=43 StartZ=0 EndX=0.875002 EndY=160.593 EndZ=0
    g5: LineSegment StartX=212.375 StartY=141.462 StartZ=0 EndX=212.375 EndY=45 EndZ=0
    g6: LineSegment StartX=212.375 StartY=45 StartZ=0 EndX=2.875 EndY=45 EndZ=0
    g7: LineSegment StartX=2.875 StartY=45 StartZ=0 EndX=2.875 EndY=159.126 EndZ=0
    g8: LineSegment StartX=2.875 StartY=159.126 StartZ=0 EndX=67.0444 EndY=179.33 EndZ=0
    g9: LineSegment StartX=67.0444 StartY=179.33 StartZ=0 EndX=212.375 EndY=141.462 EndZ=0
  constraints (21):
    c: Coincident(g-7,g0)
    c: Coincident(g0,g-4)
    c: Coincident(g0,g1)
    c: Coincident(g1,g-5)
    c: Coincident(g1,g2)
    c: Coincident(g2,g-6)
    c: Coincident(g2,g3)
    c: Coincident(g3,g-7)
    c: Coincident(g3,g4)
    c: Coincident(g4,g0)
    c: Coincident(g5,g6)
    c: Coincident(g5,g9)
    c: Coincident(g6,g7)
    c: Coincident(g7,g8)
    c: Coincident(g8,g9)
    c: Block(g9)
    c: Block(g5)
    c: Parallel(g0,g8)
    c: DistanceX(g3,g6) = 2
    c: Vertical(g7)
    c: Horizontal(g6)
FEATURE [PartDesign::Pad] Pad020
  BaseFeature = -> Pocket015
  Direction = (0,0,1)
  Length = 15
  Length2 = 10
  Profile = -> Sketch026
  ReferenceAxis = -> Sketch026 [N_Axis]
  Type = 0
FEATURE [Sketcher::SketchObject] Sketch027
  ExternalGeometry = -> [Pad020]
  FullyConstrained = true
  MapMode = 5
  Placement = pos=(0,0,2.3) rot=(0,0,1;0rad)
  Support = -> [Pad020]
  sketch-geometry (10):
    g0: LineSegment StartX=88.1 StartY=64.5 StartZ=0 EndX=88.1 EndY=66.775 EndZ=0
    g1: LineSegment StartX=88.1 StartY=66.775 StartZ=0 EndX=88.1 EndY=69.05 EndZ=0
    g2: LineSegment StartX=88.1 StartY=66.775 StartZ=0 EndX=212.375 EndY=66.775 EndZ=0
    g3: LineSegment StartX=56.525 StartY=66 StartZ=0 EndX=56.525 EndY=67.55 EndZ=0
    g4: LineSegment StartX=56.525 StartY=67.55 StartZ=0 EndX=212.375 EndY=67.55 EndZ=0
    g5: LineSegment StartX=212.375 StartY=67.55 StartZ=0 EndX=212.375 EndY=66 EndZ=0
    g6: LineSegment StartX=212.375 StartY=66 StartZ=0 EndX=56.525 EndY=66 EndZ=0
    g7: GeomPoint X=134.45 Y=66.775 Z=0
    g8: LineSegment StartX=97.625 StartY=83.55 StartZ=0 EndX=97.625 EndY=85.825 EndZ=0
    g9: LineSegment StartX=97.625 StartY=85.825 StartZ=0 EndX=97.625 EndY=88.1 EndZ=0
  constraints (29):
    c: Coincident(g-4,g0)
    c: Vertical(g0)
    c: Coincident(g0,g1)
    c: Vertical(g1)
    c: Equal(g1,g0)
    c: Coincident(g2,g0)
    c: PointOnObject(g2,g-3)
    c: Horizontal(g2)
    c: Coincident(g3,g4)
    c: Coincident(g4,g5)
    c: Coincident(g5,g6)
    c: Coincident(g6,g3)
    c: Vertical(g3)
    c: Vertical(g5)
    c: Horizontal(g4)
    c: Horizontal(g6)
    c: Symmetric(g5,g3,g7)
    c: PointOnObject(g7,g2)
    c: PointOnObject(g5,g-3)
    c: PointOnObject(g1,g-5)
    c: DistanceY(g0,g3) = 1.5
    c: DistanceX(g-6,g3) = 22
    c: Coincident(g8,g-7)
    c: Vertical(g8)
    c: Coincident(g9,g8)
    c: PointOnObject(g9,g-8)
    c: Vertical(g9)
    c: Equal(g9,g8)
    c: DistanceY(g0,g8) = 19.05  'wall_row_distance'
FEATURE [PartDesign::Pad] Pad021
  BaseFeature = -> Pad020
  Direction = (0,0,1)
  Length = 20
  Length2 = 10
  Profile = -> Sketch027
  ReferenceAxis = -> Sketch027 [N_Axis]
  Type = 3
  UpToFace = -> Pad020 [Face161]
FEATURE [PartDesign::LinearPattern] LinearPattern
  BaseFeature = -> Pad021
  Direction = -> Sketch027 [V_Axis]
  Length = 57.15
  Mode = 0
  Occurrences = 4
  Offset = 19.05
  Originals = -> [Pad021]
  expr: Length = Sketch027.Constraints.wall_row_distance * (Occurrences - 1)
FEATURE [PartDesign::Pad] Pad022
  BaseFeature = -> LinearPattern
  Direction = (-1,0,0)
  Length = 10
  Length2 = 10
  Profile = -> LinearPattern [Face164]
  Type = 2
FEATURE [PartDesign::Pad] Pad023
  BaseFeature = -> Pad022
  Direction = (-1,0,0)
  Length = 2
  Length2 = 10
  Profile = -> Pad022 [Face170]
  Type = 0
FEATURE [PartDesign::Pad] Pad024
  BaseFeature = -> Pad023
  Direction = (0,-1,0)
  Length = 10
  Length2 = 10
  Profile = -> Pad023 [Face171]
  Type = 2
FEATURE [PartDesign::Pad] Pad025
  BaseFeature = -> Pad024
  Direction = (0,1,0)
  Length = 10
  Length2 = 10
  Profile = -> Pad024 [Face179]
  Type = 2
FEATURE [PartDesign::Pocket] Pocket016
  BaseFeature = -> Pad025
  Direction = (0,0,-1)
  Length = 8
  Length2 = 5
  Profile = -> Pad025 [Face201,Face202,Face199]
  Type = 0
FEATURE [PartDesign::Pocket] Pocket017
  BaseFeature = -> Pocket016
  Direction = (0,0,-1)
  Length = 8
  Length2 = 5
  Profile = -> Pocket016 [Face200]
  Type = 0
FEATURE [PartDesign::Pad] Pad026
  BaseFeature = -> Pocket013
  Direction = (1,0,0)
  Length = 10
  Length2 = 10
  Profile = -> Pocket013 [Face117]
  Type = 2
FEATURE [PartDesign::Body] Body_3  label="plate_left"
  BaseFeature = -> baseplate_left001001_solid
  Group = -> [BaseFeature,LCS_0004,Sketch021,Pocket012,Sketch022,Pocket013,Pad026]
  Origin = -> Origin012
  Tip = -> Pocket013
FEATURE [PartDesign::Pocket] Pocket018
  BaseFeature = -> Pocket017
  Direction = (0,0,1)
  Length = 0.9
  Length2 = 5
  Profile = -> Pocket017 [Face1]
  Type = 0
FEATURE [Sketcher::SketchObject] Sketch028
  FullyConstrained = false
  MapMode = 5
  Placement = pos=(0,0,0.9) rot=(1,0,0;3.14159rad)
  Support = -> [Pocket018]
  sketch-geometry (8):
    g0: LineSegment StartX=186.641 StartY=-48.1554 StartZ=0 EndX=186.641 EndY=-65.87 EndZ=0
    g1: LineSegment StartX=186.641 StartY=-65.87 StartZ=0 EndX=203.656 EndY=-65.87 EndZ=0
    g2: LineSegment StartX=203.656 StartY=-65.87 StartZ=0 EndX=203.656 EndY=-48.1554 EndZ=0
    g3: LineSegment StartX=203.656 StartY=-48.1554 StartZ=0 EndX=186.641 EndY=-48.1554 EndZ=0
    g4: LineSegment StartX=-16.894 StartY=-28.9206 StartZ=0 EndX=-16.894 EndY=-187.952 EndZ=0
    g5: LineSegment StartX=-16.894 StartY=-187.952 StartZ=0 EndX=239.258 EndY=-187.952 EndZ=0
    g6: LineSegment StartX=239.258 StartY=-187.952 StartZ=0 EndX=239.258 EndY=-28.9206 EndZ=0
    g7: LineSegment StartX=239.258 StartY=-28.9206 StartZ=0 EndX=-16.894 EndY=-28.9206 EndZ=0
  constraints (16):
    c: Coincident(g0,g1)
    c: Coincident(g1,g2)
    c: Coincident(g2,g3)
    c: Coincident(g3,g0)
    c: Vertical(g0)
    c: Vertical(g2)
    c: Horizontal(g1)
    c: Horizontal(g3)
    c: Coincident(g4,g5)
    c: Coincident(g5,g6)
    c: Coincident(g6,g7)
    c: Coincident(g7,g4)
    c: Vertical(g4)
    c: Vertical(g6)
    c: Horizontal(g5)
    c: Horizontal(g7)
FEATURE [PartDesign::Pocket] Pocket019
  BaseFeature = -> Pocket018
  Direction = (0,0,1)
  Length = 5
  Length2 = 5
  Profile = -> Sketch028
  ReferenceAxis = -> Sketch028 [N_Axis]
  Type = 1
FEATURE [PartDesign::Pad] Pad027
  BaseFeature = -> Pocket019
  Direction = (-1,0,0)
  Length = 0.4
  Length2 = 10
  Profile = -> Pocket019 [Face8]
  Type = 0
  expr: Length = Spreadsheet.horizontal_pad
FEATURE [PartDesign::Pad] Pad028
  BaseFeature = -> Pad027
  Direction = (0,-1,0)
  Length = 0.4
  Length2 = 10
  Profile = -> Pad027 [Face6]
  Type = 0
  expr: Length = Spreadsheet.horizontal_pad
FEATURE [PartDesign::Body] plate_right
  BaseFeature = -> baseplate_right001001_solid
  Group = -> [BaseFeature001,LCS_0005,Sketch024,Pocket014,Sketch025,Pocket015,Sketch026,Pad020,Sketch027,Pad021,LinearPattern,Pad022,Pad023,Pad024,Pad025,Pocket016,Pocket017,Pocket018,Sketch028,Pocket019,Pad027,Pad028]
  Origin = -> Origin
  Tip = -> Pocket018
FEATURE [Sketcher::SketchObject] Sketch032
  AttachmentOffset = pos=(0,0,1.3) rot=(0,0,1;0rad)
  FullyConstrained = true
  MapMode = 5
  Placement = pos=(0,0,1.3) rot=(0,0,1;0rad)
  Support = -> [XY_Plane013]
  expr: .AttachmentOffset.Base.z = Spreadsheet.h_plate
  sketch-geometry (6):
    g0: LineSegment StartX=194.05 StartY=191.575 StartZ=0 EndX=333.212 EndY=191.575 EndZ=0
    g1: LineSegment StartX=333.212 StartY=190.8 StartZ=0 EndX=333.212 EndY=192.35 EndZ=0
    g2: LineSegment StartX=333.212 StartY=192.35 StartZ=0 EndX=178.212 EndY=192.35 EndZ=0
    g3: LineSegment StartX=178.212 StartY=192.35 StartZ=0 EndX=178.212 EndY=190.8 EndZ=0
    g4: LineSegment StartX=178.212 StartY=190.8 StartZ=0 EndX=333.212 EndY=190.8 EndZ=0
    g5: GeomPoint X=255.712 Y=191.575 Z=0
  constraints (14):
    c: Coincident(g1,g2)
    c: Coincident(g2,g3)
    c: Coincident(g3,g4)
    c: Coincident(g4,g1)
    c: Vertical(g1)
    c: Vertical(g3)
    c: Horizontal(g2)
    c: Horizontal(g4)
    c: Symmetric(g3,g1,g5)
    c: PointOnObject(g5,g0)
    c: Block(g0)
    c: DistanceY(g3,g3) = 1.55
    c: PointOnObject(g0,g1)
    c: DistanceX(g4,g4) = 155
FEATURE [PartDesign::FeatureBase] BaseFeature002
  BaseFeature = -> baseplate_right_v004_solid
FEATURE [Sketcher::SketchObject] Sketch029
  AttachmentOffset = pos=(0,0,10) rot=(0,0,1;0rad)
  ExternalGeometry = -> [BaseFeature002]
  FullyConstrained = true
  MapMode = 5
  Placement = pos=(0,0,10) rot=(0,0,1;0rad)
  Support = -> [XY_Plane013]
  expr: Constraints[24] = Spreadsheet.d_key
  expr: Constraints[9] = Spreadsheet.switch_hole_size
  sketch-geometry (19):
    g0: LineSegment StartX=155.753 StartY=278.77 StartZ=0 EndX=145.783 EndY=268.8 EndZ=0
    g1: LineSegment StartX=145.783 StartY=268.8 StartZ=0 EndX=155.753 EndY=258.83 EndZ=0
    g2: LineSegment StartX=155.753 StartY=258.83 StartZ=0 EndX=165.723 EndY=268.8 EndZ=0
    g3: LineSegment StartX=165.723 StartY=268.8 StartZ=0 EndX=155.753 EndY=278.77 EndZ=0
    g4: GeomPoint X=155.753 Y=268.8 Z=0
    g5: LineSegment StartX=169.224 StartY=265.3 StartZ=0 EndX=159.253 EndY=255.33 EndZ=0
    g6: LineSegment StartX=159.253 StartY=255.33 StartZ=0 EndX=169.224 EndY=245.359 EndZ=0
    g7: LineSegment StartX=169.224 StartY=245.359 StartZ=0 EndX=179.194 EndY=255.33 EndZ=0
    g8: LineSegment StartX=179.194 StartY=255.33 StartZ=0 EndX=169.224 EndY=265.3 EndZ=0
    g9: GeomPoint X=169.224 Y=255.33 Z=0
    g10: LineSegment StartX=155.753 StartY=268.8 StartZ=0 EndX=169.224 EndY=255.33 EndZ=0
    g11: LineSegment StartX=180.166 StartY=289.713 StartZ=0 EndX=170.196 EndY=279.742 EndZ=0
    g12: LineSegment StartX=170.196 StartY=279.742 StartZ=0 EndX=180.166 EndY=269.772 EndZ=0
    g13: LineSegment StartX=180.166 StartY=269.772 StartZ=0 EndX=190.136 EndY=279.742 EndZ=0
    g14: LineSegment StartX=190.136 StartY=279.742 StartZ=0 EndX=180.166 EndY=289.713 EndZ=0
    g15: GeomPoint X=180.166 Y=279.742 Z=0
    g16: LineSegment StartX=162.488 StartY=262.065 StartZ=0 EndX=180.166 EndY=279.742 EndZ=0
    g17: LineSegment StartX=179.194 StartY=255.33 StartZ=0 EndX=180.166 EndY=269.772 EndZ=0
    g18: LineSegment StartX=170.196 StartY=279.742 StartZ=0 EndX=155.753 EndY=278.77 EndZ=0
  constraints (49):
    c: Coincident(g0,g1)
    c: Coincident(g1,g2)
    c: Coincident(g2,g3)
    c: Coincident(g3,g0)
    c: Symmetric(g2,g0,g4)
    c: Equal(g0,g1)
    c: Parallel(g1,g3)
    c: Parallel(g2,g0)
    c: Perpendicular(g1,g0)
    c: Distance(g1) = 14.1
    c: Coincident(g5,g6)
    c: Coincident(g6,g7)
    c: Coincident(g7,g8)
    c: Coincident(g8,g5)
    c: Symmetric(g7,g5,g9)
    c: Equal(g5,g6)
    c: Parallel(g5,g7)
    c: Parallel(g6,g8)
    c: Perpendicular(g5,g6)
    c: Parallel(g6,g1)
    c: Coincident(g10,g4)
    c: Coincident(g10,g9)
    c: Perpendicular(g2,g10)
    c: Equal(g1,g6)
    c: Distance(g10) = 19.05
    c: Coincident(g11,g12)
    c: Coincident(g12,g13)
    c: Coincident(g13,g14)
    c: Coincident(g14,g11)
    c: Symmetric(g13,g11,g15)
    c: Parallel(g13,g11)
    c: Parallel(g12,g14)
    c: Perpendicular(g12,g11)
    c: Equal(g12,g3)
    c: Equal(g12,g11)
    c: PointOnObject(g16,g10)
    c: Coincident(g16,g15)
    c: Perpendicular(g10,g16)
    c: Perpendicular(g12,g16)
    c: Angle(g10,g-1) = 0.785398
    c: Coincident(g17,g7)
    c: Coincident(g17,g12)
    c: Coincident(g18,g11)
    c: Coincident(g18,g0)
    c: Equal(g18,g17)
    c: DistanceX(g7,g-3) = 22
    c: DistanceY(g7,g-3) = 9.97038
    c: Block(g10)
    c: Distance(g16) = 25
FEATURE [PartDesign::Pocket] Pocket020
  BaseFeature = -> BaseFeature002
  Direction = (0,0,-1)
  Length = 5
  Length2 = 5
  Profile = -> Sketch029
  ReferenceAxis = -> Sketch029 [N_Axis]
  Type = 1
FEATURE [Sketcher::SketchObject] Sketch030
  AttachmentOffset = pos=(0,0,1.3) rot=(0,0,1;0rad)
  ExternalGeometry = -> [Pocket020]
  FullyConstrained = true
  MapMode = 5
  Placement = pos=(0,0,1.3) rot=(0,0,1;0rad)
  Support = -> [XY_Plane013]
  expr: .AttachmentOffset.Base.z = Spreadsheet.h_plate
  sketch-geometry (20):
    g0: LineSegment StartX=101.875 StartY=160 StartZ=0 EndX=101.875 EndY=268.536 EndZ=0
    g1: LineSegment StartX=101.875 StartY=268.536 StartZ=0 EndX=180.166 EndY=295.713 EndZ=0
    g2: LineSegment StartX=180.166 StartY=295.713 StartZ=0 EndX=335.212 EndY=273.3 EndZ=0
    g3: LineSegment StartX=335.212 StartY=273.3 StartZ=0 EndX=335.212 EndY=160 EndZ=0
    g4: LineSegment StartX=335.212 StartY=160 StartZ=0 EndX=101.875 EndY=160 EndZ=0
    g5: LineSegment StartX=116.675 StartY=222.5 StartZ=0 EndX=116.675 EndY=166 EndZ=0
    g6: LineSegment StartX=116.675 StartY=166 StartZ=0 EndX=113.875 EndY=166 EndZ=0
    g7: LineSegment StartX=113.875 StartY=166 StartZ=0 EndX=113.875 EndY=222.5 EndZ=0
    g8: LineSegment StartX=113.875 StartY=222.5 StartZ=0 EndX=116.675 EndY=222.5 EndZ=0
    g9: GeomPoint X=115.275 Y=194.25 Z=0
    g10: LineSegment StartX=139.525 StartY=222.5 StartZ=0 EndX=139.525 EndY=166 EndZ=0
    g11: LineSegment StartX=139.525 StartY=166 StartZ=0 EndX=136.725 EndY=166 EndZ=0
    g12: LineSegment StartX=136.725 StartY=166 StartZ=0 EndX=136.725 EndY=222.5 EndZ=0
    g13: LineSegment StartX=136.725 StartY=222.5 StartZ=0 EndX=139.525 EndY=222.5 EndZ=0
    g14: GeomPoint X=138.125 Y=194.25 Z=0
    g15: LineSegment StartX=155.753 StartY=278.77 StartZ=0 EndX=153.13 EndY=286.328 EndZ=0
    g16: LineSegment StartX=0 StartY=0 StartZ=0 EndX=600 EndY=0 EndZ=0
    g17: LineSegment StartX=600 StartY=0 StartZ=0 EndX=600 EndY=600 EndZ=0
    g18: LineSegment StartX=600 StartY=600 StartZ=0 EndX=0 EndY=600 EndZ=0
    g19: LineSegment StartX=0 StartY=600 StartZ=0 EndX=0 EndY=0 EndZ=0
  constraints (59):
    c: Coincident(g0,g1)
    c: Coincident(g1,g2)
    c: Coincident(g2,g3)
    c: Vertical(g3)
    c: Coincident(g3,g4)
    c: Coincident(g4,g0)
    c: Horizontal(g4)
    c: Coincident(g5,g6)
    c: Coincident(g6,g7)
    c: Coincident(g7,g8)
    c: Coincident(g8,g5)
    c: Vertical(g5)
    c: Vertical(g7)
    c: Horizontal(g6)
    c: Horizontal(g8)
    c: Symmetric(g7,g5,g9)
    c: Coincident(g10,g11)
    c: Coincident(g11,g12)
    c: Coincident(g12,g13)
    c: Coincident(g13,g10)
    c: Vertical(g10)
    c: Vertical(g12)
    c: Horizontal(g11)
    c: Horizontal(g13)
    c: Symmetric(g12,g10,g14)
    c: DistanceX(g9,g14) = 22.85
    c: PointOnObject(g7,g13)
    c: Equal(g7,g10)
    c: Equal(g6,g11)
    c: DistanceX(g8,g8) = 2.8
    c: DistanceY(g7,g7) = 56.5
    c: DistanceY(g3,g-3) = 15
    c: DistanceX(g-3,g3) = 8
    c: DistanceY(g0,g6) = 6
    c: DistanceX(g0,g6) = 12
    c: DistanceY(g-5,g1) = 6
    c: DistanceX(g1,g-5) = 0
    c: Coincident(g15,g-6)
    c: PointOnObject(g15,g1)
    c: Perpendicular(g1,g15)
    c: Distance(g15) = 8
    c: Coincident(g16,g17)
    c: Coincident(g17,g18)
    c: Coincident(g18,g19)
    c: Coincident(g19,g16)
    c: Horizontal(g16)
    c: Horizontal(g18)
    c: Vertical(g17)
    c: Vertical(g19)
    c: Distance(g17,g19) = 600
    c: Distance(g16,g18) = 600
    c: Coincident(g16,g-1)
    c: Block(g3)
    c: Block(g2)
    c: Block(g1)
    c: Block(g12)
    c: Vertical(g0)
    c: DistanceY(g-7,g2) = 8
    c: DistanceX(g10,g-4) = 45
FEATURE [PartDesign::Pocket] Pocket021
  BaseFeature = -> Pocket020
  Direction = (0,0,-1)
  Length = 5
  Length2 = 5
  Profile = -> Sketch030
  ReferenceAxis = -> Sketch030 [N_Axis]
  Type = 1
FEATURE [Sketcher::SketchObject] Sketch031
  AttachmentOffset = pos=(0,0,1.3) rot=(0,0,1;0rad)
  ExternalGeometry = -> [Sketch030]
  FullyConstrained = true
  MapMode = 5
  Placement = pos=(0,0,1.3) rot=(0,0,1;0rad)
  Support = -> [XY_Plane013]
  expr: .AttachmentOffset.Base.z = Spreadsheet.h_plate
  expr: Constraints[39] = Spreadsheet.d_wall_out
  sketch-geometry (16):
    g0: LineSegment StartX=101.875 StartY=160 StartZ=0 EndX=101.875 EndY=268.536 EndZ=0
    g1: LineSegment StartX=101.875 StartY=268.536 StartZ=0 EndX=180.166 EndY=295.713 EndZ=0
    g2: LineSegment StartX=180.166 StartY=295.713 StartZ=0 EndX=335.212 EndY=273.3 EndZ=0
    g3: LineSegment StartX=335.212 StartY=273.3 StartZ=0 EndX=335.212 EndY=160 EndZ=0
    g4: LineSegment StartX=335.212 StartY=160 StartZ=0 EndX=101.875 EndY=160 EndZ=0
    g5: LineSegment StartX=103.875 StartY=162 StartZ=0 EndX=103.875 EndY=267.23 EndZ=0
    g6: LineSegment StartX=103.875 StartY=267.23 StartZ=0 EndX=180.166 EndY=293.713 EndZ=0
    g7: LineSegment StartX=180.166 StartY=293.713 StartZ=0 EndX=333.212 EndY=271.589 EndZ=0
    g8: LineSegment StartX=333.212 StartY=271.589 StartZ=0 EndX=333.212 EndY=162 EndZ=0
    g9: LineSegment StartX=333.212 StartY=162 StartZ=0 EndX=103.875 EndY=162 EndZ=0
    g10: LineSegment StartX=103.875 StartY=162 StartZ=0 EndX=103.875 EndY=160 EndZ=0
    g11: LineSegment StartX=103.875 StartY=162 StartZ=0 EndX=101.875 EndY=162 EndZ=0
    g12: LineSegment StartX=103.875 StartY=267.23 StartZ=0 EndX=101.875 EndY=267.23 EndZ=0
    g13: LineSegment StartX=180.166 StartY=295.713 StartZ=0 EndX=180.166 EndY=293.713 EndZ=0
    g14: LineSegment StartX=333.212 StartY=271.589 StartZ=0 EndX=335.212 EndY=271.589 EndZ=0
    g15: LineSegment StartX=333.212 StartY=162 StartZ=0 EndX=335.212 EndY=162 EndZ=0
  constraints (42):
    c: Coincident(g-4,g0)
    c: Coincident(g0,g-7)
    c: Coincident(g0,g1)
    c: Coincident(g1,g-7)
    c: Coincident(g1,g2)
    c: Coincident(g2,g-6)
    c: Coincident(g2,g3)
    c: Coincident(g3,g-5)
    c: Coincident(g3,g4)
    c: Coincident(g4,g0)
    c: Coincident(g5,g6)
    c: Coincident(g5,g9)
    c: Coincident(g6,g7)
    c: Coincident(g7,g8)
    c: Coincident(g8,g9)
    c: Coincident(g10,g5)
    c: PointOnObject(g10,g4)
    c: Vertical(g10)
    c: Coincident(g11,g5)
    c: PointOnObject(g11,g0)
    c: Horizontal(g11)
    c: Equal(g11,g10)
    c: Coincident(g12,g5)
    c: PointOnObject(g12,g0)
    c: Coincident(g13,g1)
    c: Coincident(g6,g13)
    c: Vertical(g13)
    c: Horizontal(g12)
    c: Coincident(g14,g7)
    c: PointOnObject(g14,g3)
    c: Horizontal(g14)
    c: Parallel(g7,g2)
    c: Coincident(g15,g8)
    c: PointOnObject(g15,g3)
    c: Horizontal(g15)
    c: Equal(g15,g14)
    c: Equal(g14,g13)
    c: Equal(g13,g12)
    c: Equal(g12,g11)
    c: DistanceX(g11,g11) = 2
    c: Horizontal(g9)
    c: Parallel(g6,g1)
FEATURE [PartDesign::Pad] Pad029
  BaseFeature = -> Pocket021
  Direction = (0,0,1)
  Length = 15
  Length2 = 10
  Profile = -> Sketch031
  ReferenceAxis = -> Sketch031 [N_Axis]
  Type = 0
  expr: Length = Spreadsheet.h_wall_out
FEATURE [PartDesign::Pad] Pad030
  BaseFeature = -> Pad029
  Direction = (0,0,1)
  Length = 10
  Length2 = 10
  Profile = -> Sketch032
  ReferenceAxis = -> Sketch032 [N_Axis]
  Type = 3
  UpToFace = -> Pad029 [Face161]
FEATURE [PartDesign::LinearPattern] LinearPattern001
  BaseFeature = -> Pad030
  Direction = -> Y_Axis013
  Length = 57.15
  Mode = 1
  Occurrences = 4
  Offset = 19.05
  Originals = -> [Pad030]
  expr: Offset = Spreadsheet.d_key
FEATURE [PartDesign::Pad] Pad031
  BaseFeature = -> LinearPattern001
  Direction = (-1,0,0)
  Length = 2
  Length2 = 10
  Profile = -> LinearPattern001 [Face167]
  Type = 0
  expr: Length = Spreadsheet.d_wall_out
FEATURE [PartDesign::Pad] Pad032
  BaseFeature = -> Pad031
  Direction = (0,-1,0)
  Length = 10
  Length2 = 10
  Profile = -> Pad031 [Face169]
  Type = 2
FEATURE [Sketcher::SketchObject] Sketch033
  AttachmentOffset = pos=(0,0,1.5) rot=(0,0,1;0rad)
  ExternalGeometry = -> [Pad032]
  FullyConstrained = true
  MapMode = 5
  Placement = pos=(0,0,1.5) rot=(0,0,1;0rad)
  Support = -> [XY_Plane013]
  expr: .AttachmentOffset.Base.z = Spreadsheet.h_plate
  expr: Constraints[11] = Spreadsheet.d_wall_out
  expr: Constraints[25] = Spreadsheet.d_wall_out
  sketch-geometry (10):
    g0: LineSegment StartX=178.212 StartY=230.45 StartZ=0 EndX=103.875 EndY=267.23 EndZ=0
    g1: LineSegment StartX=103.875 StartY=267.23 StartZ=0 EndX=103.875 EndY=264.999 EndZ=0
    g2: LineSegment StartX=103.875 StartY=264.999 StartZ=0 EndX=178.212 EndY=228.219 EndZ=0
    g3: LineSegment StartX=178.212 StartY=228.219 StartZ=0 EndX=178.212 EndY=230.45 EndZ=0
    g4: LineSegment StartX=178.212 StartY=230.45 StartZ=0 EndX=177.326 EndY=228.657 EndZ=0
    g5: LineSegment StartX=176.212 StartY=249.5 StartZ=0 EndX=215.014 EndY=288.675 EndZ=0
    g6: LineSegment StartX=215.014 StartY=288.675 StartZ=0 EndX=217.8 EndY=288.273 EndZ=0
    g7: LineSegment StartX=217.8 StartY=288.273 StartZ=0 EndX=179.027 EndY=249.5 EndZ=0
    g8: LineSegment StartX=179.027 StartY=249.5 StartZ=0 EndX=176.212 EndY=249.5 EndZ=0
    g9: LineSegment StartX=179.027 StartY=249.5 StartZ=0 EndX=177.606 EndY=250.907 EndZ=0
  constraints (27):
    c: Coincident(g-3,g0)
    c: Coincident(g0,g-4)
    c: Coincident(g0,g1)
    c: Vertical(g1)
    c: Coincident(g1,g2)
    c: Coincident(g2,g3)
    c: Coincident(g3,g0)
    c: Vertical(g3)
    c: Coincident(g4,g0)
    c: PointOnObject(g4,g2)
    c: Perpendicular(g2,g4)
    c: Distance(g4) = 2
    c: Equal(g1,g3)
    c: Coincident(g-5,g5)
    c: PointOnObject(g5,g-6)
    c: Coincident(g5,g6)
    c: PointOnObject(g6,g-6)
    c: Coincident(g6,g7)
    c: PointOnObject(g7,g-5)
    c: Coincident(g7,g8)
    c: Coincident(g8,g5)
    c: Equal(g8,g6)
    c: Coincident(g9,g7)
    c: PointOnObject(g9,g5)
    c: Perpendicular(g5,g9)
    c: Distance(g9) = 2
    c: Angle(g-1,g7) = 0.785398
FEATURE [PartDesign::Pad] Pad033
  BaseFeature = -> Pad032
  Direction = (0,0,1)
  Length = 8
  Length2 = 10
  Profile = -> Sketch033
  ReferenceAxis = -> Sketch033 [N_Axis]
  Type = 0
  expr: Length = Spreadsheet.h_wall_in
FEATURE [PartDesign::Pocket] Pocket022
  BaseFeature = -> Pad033
  Direction = (0,0,-1)
  Length = 0
  Length2 = 5
  Profile = -> Pad033 [Face201]
  Type = 3
  UpToFace = -> Pad033 [Face202]
FEATURE [PartDesign::Body] Body003  label="plate_right_v2"
  BaseFeature = -> baseplate_right_v004_solid
  Group = -> [BaseFeature002,Sketch029,Pocket020,Sketch030,Pocket021,Sketch031,Pad029,Sketch032,Pad030,LinearPattern001,Pad031,Pad032,Sketch033,Pad033,Pocket022]
  Origin = -> Origin013
  Tip = -> Pocket022
PROVENANCE & LICENSES
A FreeCAD (.FCStd) document from a public repository crawl; recipes are the document's own serialized feature recipes (and, for linked parts, companion documents' recipes).
License: as declared in the source repository (recorded in the dataset sidecar).
